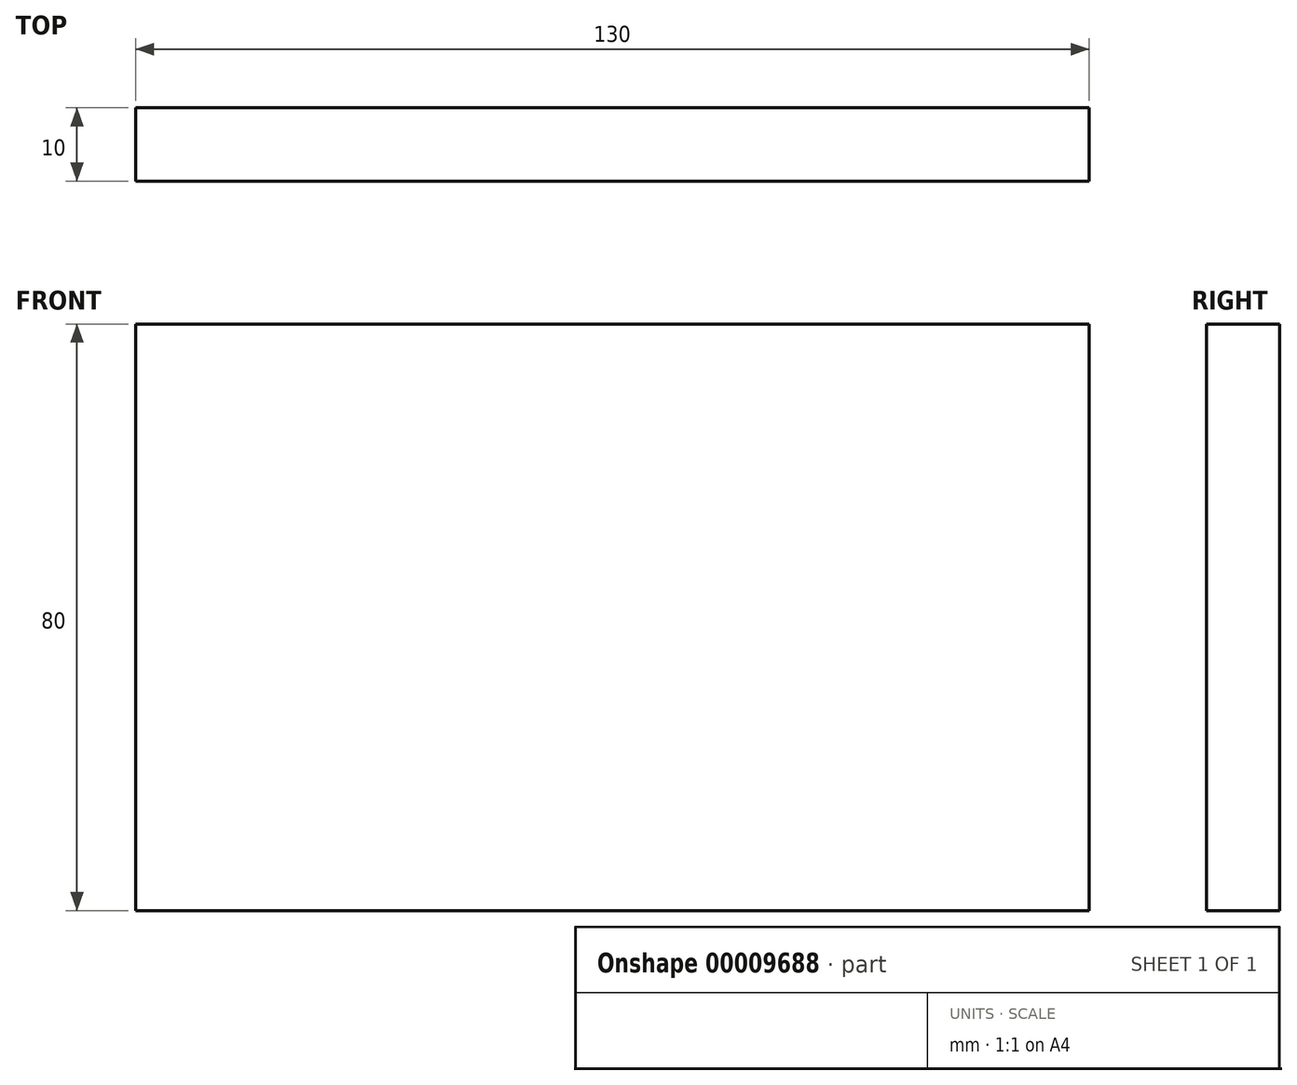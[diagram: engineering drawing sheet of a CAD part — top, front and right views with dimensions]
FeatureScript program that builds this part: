
annotation { "Feature Type Name" : "Feature", "Feature Type Description" : "" }
export const myFeature = defineFeature(function(context is Context, id is Id, definition is map)
    precondition{}
    {
        {
            var Q0;
            Q0=qCreatedBy(makeId("Front.planeOp"),FACE);
            var sketch = newSketch(context, id + "F0", { "sketchPlane" : qUnion([Q0])});
            skLineSegment(sketch, "E0.rect.bottom", {"start": v(-65, 40) * mm, "end": v(65, 40) * mm});
            skLineSegment(sketch, "E0.rect.top", {"start": v(-65, -40) * mm, "end": v(65, -40) * mm});
            skLineSegment(sketch, "E0.rect.left", {"start": v(-65, 40) * mm, "end": v(-65, -40) * mm});
            skLineSegment(sketch, "E0.rect.right", {"start": v(65, 40) * mm, "end": v(65, -40) * mm});
            skPoint(sketch, "E0.rect.middle", {"position": v(0, 0) * mm});
            skSolve(sketch);
        }
        {
            var Q0;
            Q0 = qSketchRegion(id + "F0", true);
            extrude(context, id + "F1", {"entities" : qUnion([Q0]), "depth" : 10 * mm});
        }
    });
